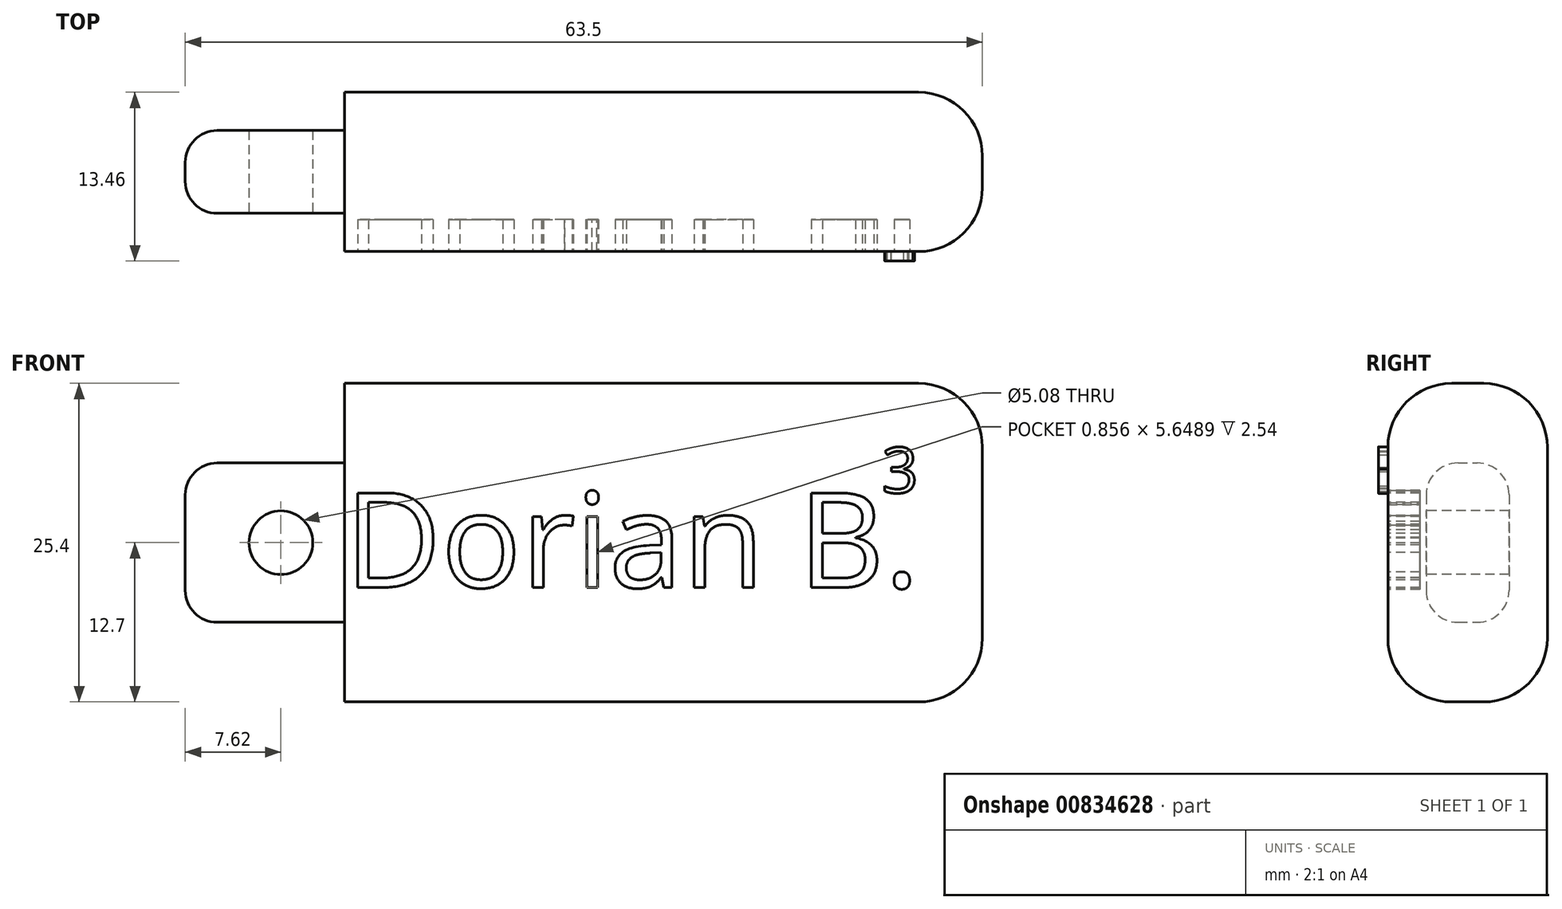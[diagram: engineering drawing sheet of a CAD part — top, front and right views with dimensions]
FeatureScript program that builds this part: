
annotation { "Feature Type Name" : "Feature", "Feature Type Description" : "" }
export const myFeature = defineFeature(function(context is Context, id is Id, definition is map)
    precondition{}
    {
        {
            var Q0;
            Q0=qCreatedBy(makeId("Front.planeOp"),FACE);
            var sketch = newSketch(context, id + "F0", { "sketchPlane" : qUnion([Q0])});
            skLineSegment(sketch, "E0.bottom", {"start": v(0, 0) * mm, "end": v(50.8, 0) * mm});
            skLineSegment(sketch, "E0.top", {"start": v(0, -25.4) * mm, "end": v(50.8, -25.4) * mm});
            skLineSegment(sketch, "E0.left", {"start": v(0, 0) * mm, "end": v(0, -25.4) * mm});
            skLineSegment(sketch, "E0.right", {"start": v(50.8, 0) * mm, "end": v(50.8, -25.4) * mm});
            skSolve(sketch);
        }
        {
            var Q0;
            Q0 = qSketchRegion(id + "F0", true);
            extrude(context, id + "F1", {"entities" : qUnion([Q0]), "depth" : 12.7 * mm, "offsetDistance" : 25.4 * mm});
        }
        {
            var Q0;
            Q0=makeQuery(id+"F1.opExtrude","CAP_EDGE",EDGE,{"disambiguationData":[OSD([sQuery(id+"F0.wireOp",EDGE,"E0.bottom")])],"isStart":false});
            var Q1;
            Q1=makeQuery(id+"F1.opExtrude","CAP_EDGE",EDGE,{"disambiguationData":[OSD([sQuery(id+"F0.wireOp",EDGE,"E0.bottom")])],"isStart":true});
            var Q2;
            Q2=makeQuery(id+"F1.opExtrude","SWEPT_EDGE",EDGE,{"disambiguationData":[OSD([sQuery(id+"F0.wireOp",EDGE,"E0.bottom"),sQuery(id+"F0.wireOp",EDGE,"E0.right")])]});
            var Q3;
            Q3=makeQuery(id+"F1.opExtrude","CAP_EDGE",EDGE,{"disambiguationData":[OSD([sQuery(id+"F0.wireOp",EDGE,"E0.right")])],"isStart":true});
            var Q4;
            Q4=makeQuery(id+"F1.opExtrude","SWEPT_EDGE",EDGE,{"disambiguationData":[OSD([sQuery(id+"F0.wireOp",EDGE,"E0.top"),sQuery(id+"F0.wireOp",EDGE,"E0.right")])]});
            var Q5;
            Q5=makeQuery(id+"F1.opExtrude","CAP_EDGE",EDGE,{"disambiguationData":[OSD([sQuery(id+"F0.wireOp",EDGE,"E0.right")])],"isStart":false});
            var Q6;
            Q6=makeQuery(id+"F1.opExtrude","CAP_EDGE",EDGE,{"disambiguationData":[OSD([sQuery(id+"F0.wireOp",EDGE,"E0.top")])],"isStart":true});
            var Q7;
            Q7=makeQuery(id+"F1.opExtrude","CAP_EDGE",EDGE,{"disambiguationData":[OSD([sQuery(id+"F0.wireOp",EDGE,"E0.top")])],"isStart":false});
            fillet(context, id + "F2", {"entities" : qUnion([Q0, Q1, Q2, Q3, Q4, Q5, Q6, Q7]), "radius" : 5.08 * mm, "tangentPropagation" : true, "allowEdgeOverflow" : false});
        }
        {
            var Q0;
            Q0=makeQuery(id+"F1.opExtrude","SWEPT_FACE",FACE,{"disambiguationData":[OSD([sQuery(id+"F0.wireOp",EDGE,"E0.left")])]});
            var sketch = newSketch(context, id + "F3", { "sketchPlane" : qUnion([Q0])});
            skLineSegment(sketch, "E1.bottom", {"start": v(9.65, -6.35) * mm, "end": v(3.05, -6.35) * mm});
            skLineSegment(sketch, "E1.top", {"start": v(9.65, -19.05) * mm, "end": v(3.05, -19.05) * mm});
            skLineSegment(sketch, "E1.left", {"start": v(9.65, -6.35) * mm, "end": v(9.65, -19.05) * mm});
            skLineSegment(sketch, "E1.right", {"start": v(3.05, -6.35) * mm, "end": v(3.05, -19.05) * mm});
            skSolve(sketch);
        }
        {
            var Q0;
            Q0 = qSketchRegion(id + "F3", true);
            extrude(context, id + "F4", {"entities" : qUnion([Q0]), "operationType" : NewBodyOperationType.ADD, "depth" : 12.7 * mm, "offsetDistance" : 25.4 * mm});
        }
        {
            var Q0;
            Q0=makeQuery(id+"F4.opExtrude","SWEPT_EDGE",EDGE,{"disambiguationData":[OSD([sQuery(id+"F3.wireOp",EDGE,"E1.bottom"),sQuery(id+"F3.wireOp",EDGE,"E1.right")])]});
            var Q1;
            Q1=makeQuery(id+"F4.opExtrude","SWEPT_EDGE",EDGE,{"disambiguationData":[OSD([sQuery(id+"F3.wireOp",EDGE,"E1.top"),sQuery(id+"F3.wireOp",EDGE,"E1.right")])]});
            var Q2;
            Q2=makeQuery(id+"F4.opExtrude","SWEPT_EDGE",EDGE,{"disambiguationData":[OSD([sQuery(id+"F3.wireOp",EDGE,"E1.top"),sQuery(id+"F3.wireOp",EDGE,"E1.left")])]});
            var Q3;
            Q3=makeQuery(id+"F4.opExtrude","SWEPT_EDGE",EDGE,{"disambiguationData":[OSD([sQuery(id+"F3.wireOp",EDGE,"E1.bottom"),sQuery(id+"F3.wireOp",EDGE,"E1.left")])]});
            var Q4;
            Q4=makeQuery(id+"F4.opExtrude","CAP_EDGE",EDGE,{"disambiguationData":[OSD([sQuery(id+"F3.wireOp",EDGE,"E1.left")])],"isStart":false});
            var Q5;
            Q5=makeQuery(id+"F4.opExtrude","CAP_EDGE",EDGE,{"disambiguationData":[OSD([sQuery(id+"F3.wireOp",EDGE,"E1.right")])],"isStart":false});
            var Q6;
            Q6=makeQuery(id+"F4.opExtrude","CAP_EDGE",EDGE,{"disambiguationData":[OSD([sQuery(id+"F3.wireOp",EDGE,"E1.top")])],"isStart":false});
            var Q7;
            Q7=makeQuery(id+"F4.opExtrude","CAP_EDGE",EDGE,{"disambiguationData":[OSD([sQuery(id+"F3.wireOp",EDGE,"E1.bottom")])],"isStart":false});
            fillet(context, id + "F5", {"entities" : qUnion([Q0, Q1, Q2, Q3, Q4, Q5, Q6, Q7]), "radius" : 2.54 * mm, "tangentPropagation" : true, "allowEdgeOverflow" : false});
        }
        {
            var Q0;
            Q0=makeQuery(id+"F4.opExtrude","SWEPT_FACE",FACE,{"disambiguationData":[OSD([sQuery(id+"F3.wireOp",EDGE,"E1.left")])]});
            var sketch = newSketch(context, id + "F6", { "sketchPlane" : qUnion([Q0])});
            skPoint(sketch, "E2", {"position": v(-5.08, -12.7) * mm});
            skPoint(sketch, "E2.positionSnap0", {"position": v(-5.08, -8.9) * mm});
            skPoint(sketch, "E2.positionSnap1", {"position": v(0, -12.7) * mm});
            skSolve(sketch);
        }
        {
            var Q0;
            Q0=sQuery(id+"F6.wireOp",VERTEX,"E2");
            var Q1;
            Q1=makeQuery(id+"F1.opExtrude","SWEPT_BODY",BODY,{"disambiguationData":[OSD([sQuery(id+"F0.wireOp",EDGE,"E0.bottom"),sQuery(id+"F0.wireOp",EDGE,"E0.top"),sQuery(id+"F0.wireOp",EDGE,"E0.left"),sQuery(id+"F0.wireOp",EDGE,"E0.right")])]});
            hole(context, id + "F7", {"style" : HoleStyle.SIMPLE, "endStyle" : HoleEndStyle.THROUGH, "holeDiameter" : 5.08 * mm, "majorDiameter" : 6.35 * mm, "isTappedThrough" : true, "tappedDepth" : 12.7 * mm, "tapClearance" : 3, "locations" : qUnion([Q0]), "scope" : qUnion([Q1])});
        }
        {
            var Q0;
            Q0=makeQuery(id+"F1.opExtrude","CAP_FACE",FACE,{"disambiguationData":[OSD([sQuery(id+"F0.wireOp",EDGE,"E0.bottom"),sQuery(id+"F0.wireOp",EDGE,"E0.top"),sQuery(id+"F0.wireOp",EDGE,"E0.left"),sQuery(id+"F0.wireOp",EDGE,"E0.right")])],"isStart":false});
            var sketch = newSketch(context, id + "F8", { "sketchPlane" : qUnion([Q0])});
            skText(sketch, "E3", { "text": "Dorian B.\n", "fontName": "OpenSans-Regular.ttf"});
            const initialGuessF8  = {"E3": [0, -0.01627, 1, 0, 0.0076]};
            skSetInitialGuess(sketch, initialGuessF8);
            skSolve(sketch);
        }
        {
            var Q0;
            Q0 = qSketchRegion(id + "F8", true);
            extrude(context, id + "F9", {"entities" : qUnion([Q0]), "operationType" : NewBodyOperationType.REMOVE, "oppositeDirection" : true, "depth" : 2.54 * mm, "offsetDistance" : 25.4 * mm});
        }
        {
            var Q0;
            {var subQ0=sQuery(id+"F0.wireOp",EDGE,"E0.right");var subQ1=sQuery(id+"F0.wireOp",EDGE,"E0.bottom");var subQ2=sQuery(id+"F0.wireOp",EDGE,"E0.left");var subQ3=sQuery(id+"F0.wireOp",EDGE,"E0.top");Q0=makeQuery(id+"F9.boolean.opBoolean","SPLIT",FACE,{"disambiguationData":[TD([makeQuery(id+"F1.opExtrude","SWEPT_FACE",FACE,{"disambiguationData":[OSD([subQ2])]})])],"derivedFrom":makeQuery(id+"F1.opExtrude","CAP_FACE",FACE,{"disambiguationData":[OSD([subQ1,subQ3,subQ2,subQ0])],"isStart":false})});}
            var sketch = newSketch(context, id + "F10", { "sketchPlane" : qUnion([Q0])});
            skText(sketch, "E4", { "text": "3\n", "fontName": "OpenSans-Regular.ttf"});
            const initialGuessF10  = {"E4": [0.04278, -0.00873, 1, 0, 0.00365]};
            skSetInitialGuess(sketch, initialGuessF10);
            skSolve(sketch);
        }
        {
            var Q0;
            Q0 = qSketchRegion(id + "F10", true);
            extrude(context, id + "F11", {"entities" : qUnion([Q0]), "operationType" : NewBodyOperationType.ADD, "depth" : 0.76 * mm, "offsetDistance" : 25.4 * mm});
        }
    });
